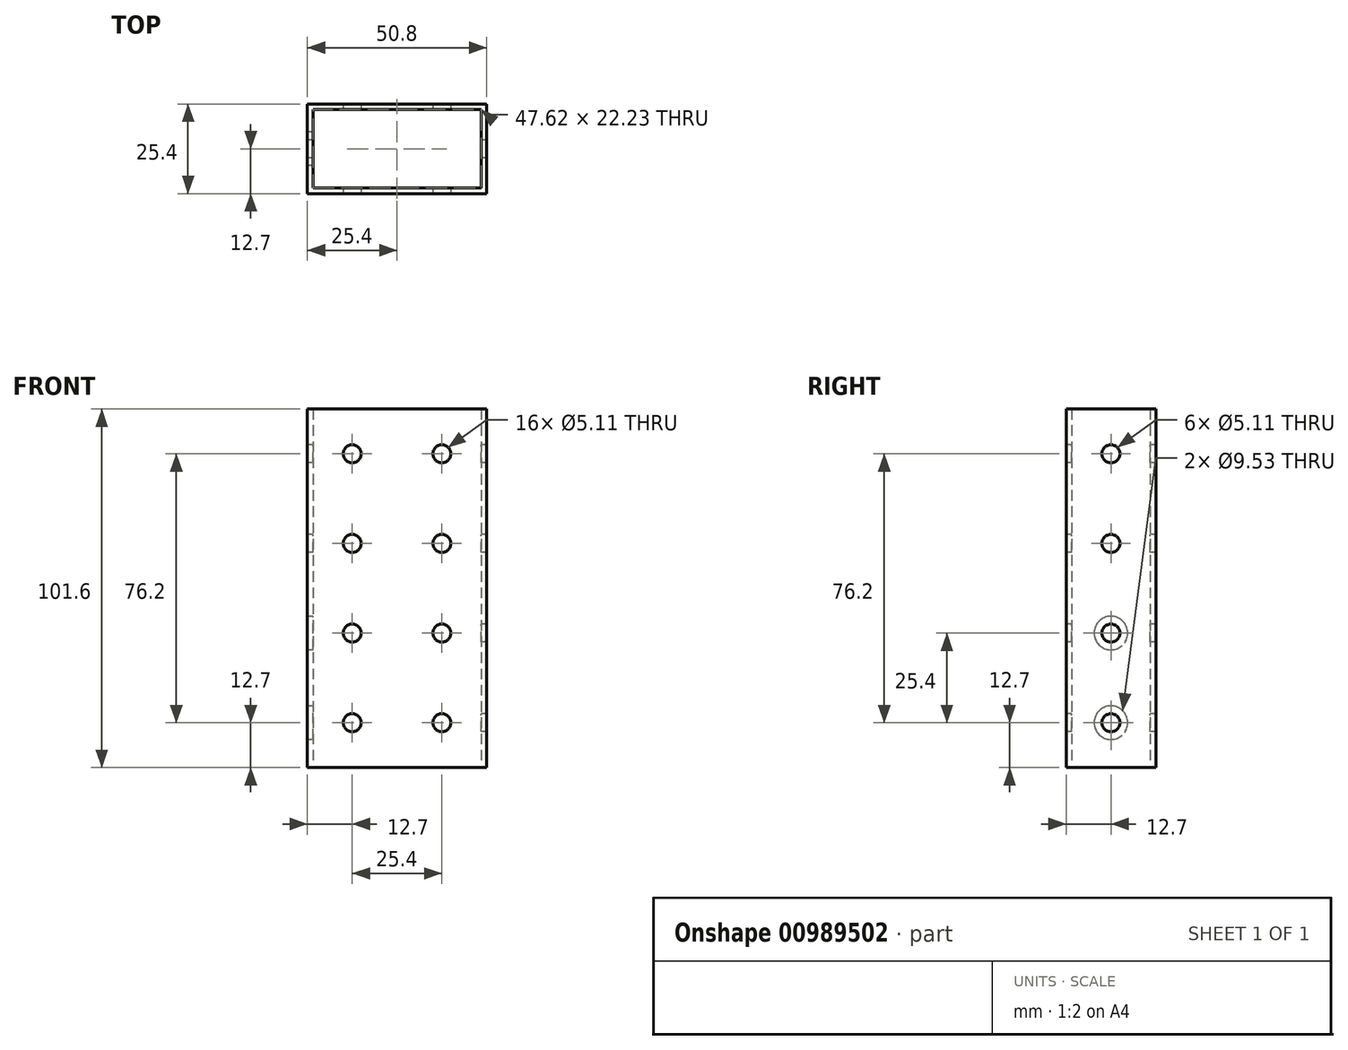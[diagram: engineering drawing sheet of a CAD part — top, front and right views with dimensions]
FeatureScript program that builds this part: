
annotation { "Feature Type Name" : "Feature", "Feature Type Description" : "" }
export const myFeature = defineFeature(function(context is Context, id is Id, definition is map)
    precondition{}
    {
        {
            var Q0;
            Q0=qCreatedBy(makeId("Top.planeOp"),FACE);
            var sketch = newSketch(context, id + "F0", { "sketchPlane" : qUnion([Q0])});
            skLineSegment(sketch, "E0.bottom", {"start": v(25.4, 12.7) * mm, "end": v(-25.4, 12.7) * mm});
            skLineSegment(sketch, "E0.top", {"start": v(25.4, -12.7) * mm, "end": v(-25.4, -12.7) * mm});
            skLineSegment(sketch, "E0.left", {"start": v(25.4, 12.7) * mm, "end": v(25.4, -12.7) * mm});
            skLineSegment(sketch, "E0.right", {"start": v(-25.4, 12.7) * mm, "end": v(-25.4, -12.7) * mm});
            skPoint(sketch, "E0.middle", {"position": v(0, 0) * mm});
            skLineSegment(sketch, "E1.0", {"start": v(23.81, 11.11) * mm, "end": v(-23.81, 11.11) * mm});
            skLineSegment(sketch, "E1.1", {"start": v(23.81, 11.11) * mm, "end": v(23.81, -11.11) * mm});
            skLineSegment(sketch, "E1.2", {"start": v(23.81, -11.11) * mm, "end": v(-23.81, -11.11) * mm});
            skLineSegment(sketch, "E1.3", {"start": v(-23.81, 11.11) * mm, "end": v(-23.81, -11.11) * mm});
            skSolve(sketch);
        }
        {
            var Q0;
            Q0 = qSketchRegion(id + "F0", true);
            extrude(context, id + "F1", {"entities" : qUnion([Q0]), "depth" : 101.6 * mm, "offsetDistance" : 25.4 * mm});
        }
        {
            var Q0;
            Q0=makeQuery(id+"F1.opExtrude","SWEPT_FACE",FACE,{"disambiguationData":[OSD([sQuery(id+"F0.wireOp",EDGE,"E0.top")])]});
            var sketch = newSketch(context, id + "F2", { "sketchPlane" : qUnion([Q0])});
            skCircle(sketch, "E2", {"center": v(-12.7, 12.7) * mm, "radius": 2.55 * mm});
            skCircle(sketch, "E3.0.1.0", {"center": v(-12.7, 38.1) * mm, "radius": 2.55 * mm});
            skCircle(sketch, "E3.0.2.0", {"center": v(-12.7, 63.5) * mm, "radius": 2.55 * mm});
            skCircle(sketch, "E3.0.3.0", {"center": v(-12.7, 88.9) * mm, "radius": 2.55 * mm});
            skCircle(sketch, "E3.1.0.0", {"center": v(12.7, 12.7) * mm, "radius": 2.55 * mm});
            skCircle(sketch, "E3.1.1.0", {"center": v(12.7, 38.1) * mm, "radius": 2.55 * mm});
            skCircle(sketch, "E3.1.2.0", {"center": v(12.7, 63.5) * mm, "radius": 2.55 * mm});
            skCircle(sketch, "E3.1.3.0", {"center": v(12.7, 88.9) * mm, "radius": 2.55 * mm});
            skLineSegment(sketch, "E3.direction1", {"start": v(-12.7, 12.7) * mm, "end": v(12.7, 12.7) * mm, "construction": true});
            skLineSegment(sketch, "E3.direction2", {"start": v(-12.7, 12.7) * mm, "end": v(-12.7, 38.1) * mm, "construction": true});
            skSolve(sketch);
        }
        {
            var Q0;
            Q0 = qSketchRegion(id + "F2", true);
            extrude(context, id + "F3", {"entities" : qUnion([Q0]), "operationType" : NewBodyOperationType.REMOVE, "oppositeDirection" : true, "depth" : 25.4 * mm, "offsetDistance" : 25.4 * mm});
        }
        {
            var Q0;
            Q0=makeQuery(id+"F1.opExtrude","SWEPT_FACE",FACE,{"disambiguationData":[OSD([sQuery(id+"F0.wireOp",EDGE,"E0.right")])]});
            var sketch = newSketch(context, id + "F4", { "sketchPlane" : qUnion([Q0])});
            skCircle(sketch, "E4", {"center": v(0, 88.9) * mm, "radius": 2.55 * mm});
            skCircle(sketch, "E5.0.1.0", {"center": v(0, 63.5) * mm, "radius": 2.55 * mm});
            skCircle(sketch, "E5.0.2.0", {"center": v(0, 38.1) * mm, "radius": 2.55 * mm});
            skCircle(sketch, "E5.0.3.0", {"center": v(0, 12.7) * mm, "radius": 2.55 * mm});
            skLineSegment(sketch, "E5.direction1", {"start": v(0, 88.9) * mm, "end": v(25.4, 88.9) * mm, "construction": true});
            skLineSegment(sketch, "E5.direction2", {"start": v(0, 88.9) * mm, "end": v(0, 63.5) * mm, "construction": true});
            skSolve(sketch);
        }
        {
            var Q0;
            Q0 = qSketchRegion(id + "F4", true);
            extrude(context, id + "F5", {"entities" : qUnion([Q0]), "operationType" : NewBodyOperationType.REMOVE, "endBound" : BoundingType.THROUGH_ALL, "oppositeDirection" : true, "depth" : 25.4 * mm, "offsetDistance" : 25.4 * mm});
        }
        {
            var Q0;
            Q0=makeQuery(id+"F1.opExtrude","SWEPT_FACE",FACE,{"disambiguationData":[OSD([sQuery(id+"F0.wireOp",EDGE,"E0.right")])]});
            var sketch = newSketch(context, id + "F6", { "sketchPlane" : qUnion([Q0])});
            skCircle(sketch, "E6", {"center": v(0, 12.7) * mm, "radius": 4.76 * mm});
            skCircle(sketch, "E7", {"center": v(0, 38.1) * mm, "radius": 4.76 * mm});
            skSolve(sketch);
        }
        {
            var Q0;
            Q0 = qSketchRegion(id + "F6", true);
            extrude(context, id + "F7", {"entities" : qUnion([Q0]), "operationType" : NewBodyOperationType.REMOVE, "oppositeDirection" : true, "depth" : 3.17 * mm, "offsetDistance" : 25.4 * mm});
        }
    });
